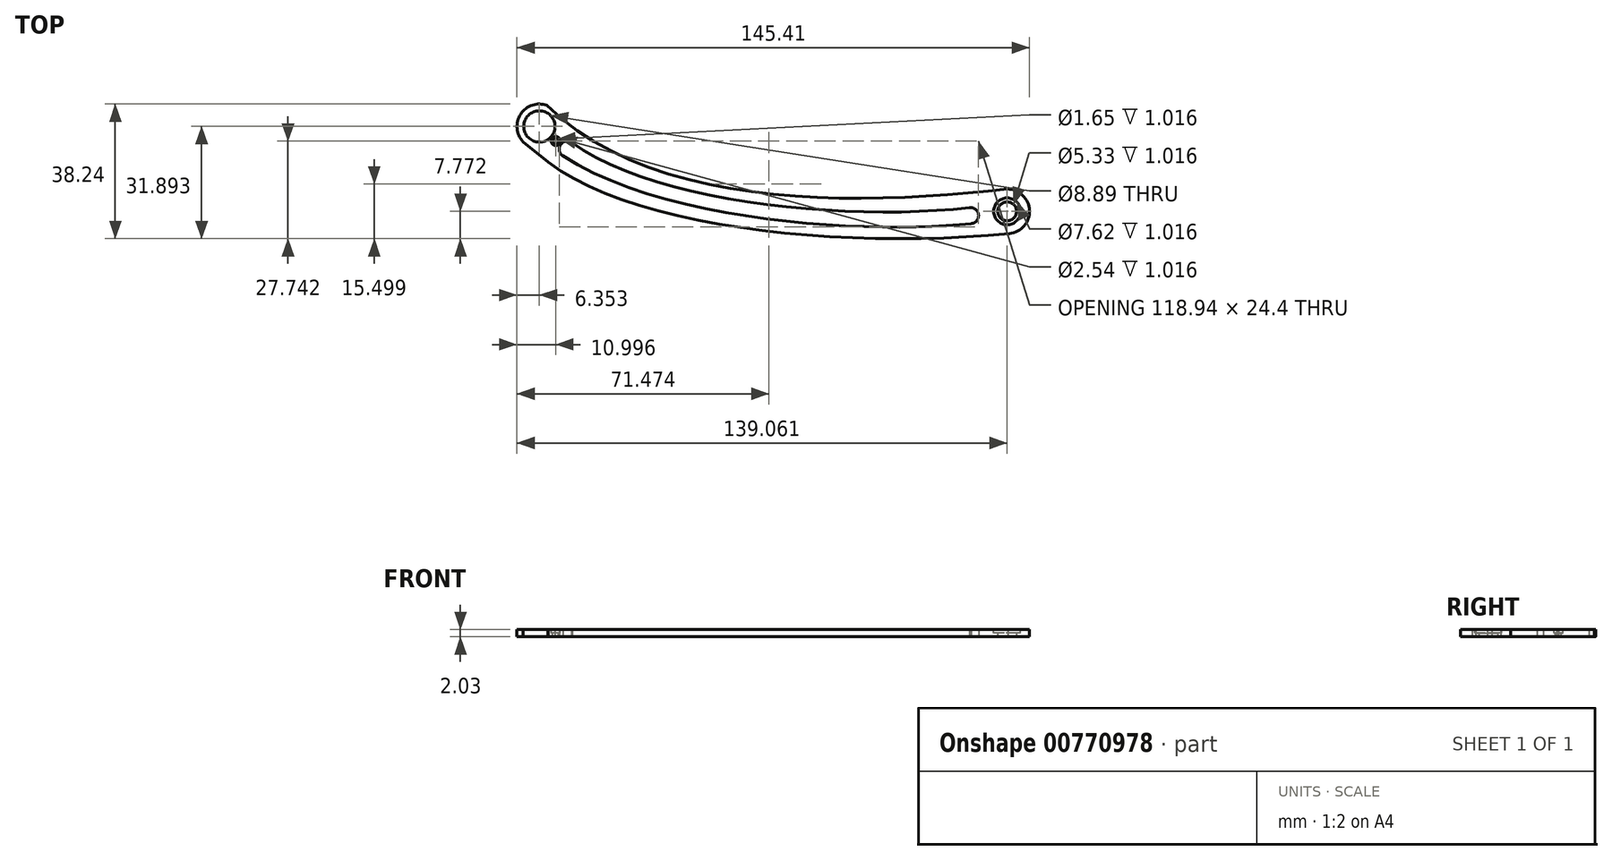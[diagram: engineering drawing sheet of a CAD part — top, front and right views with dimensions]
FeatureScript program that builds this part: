
annotation { "Feature Type Name" : "Feature", "Feature Type Description" : "" }
export const myFeature = defineFeature(function(context is Context, id is Id, definition is map)
    precondition{}
    {
        {
            var Q0;
            Q0=qCreatedBy(makeId("Top.planeOp"),FACE);
            var sketch = newSketch(context, id + "F0", { "sketchPlane" : qUnion([Q0])});
            skArc(sketch, "E0", {"start": v(-15, -65.15) * mm, "mid": v(-9.32, -58.57) * mm, "end": v(-15.52, -52.49) * mm});
            skArc(sketch, "E1", {"start": v(-146.22, -28.74) * mm, "mid": v(-153.68, -31.23) * mm, "end": v(-153, -39.07) * mm});
            skFitSpline(sketch, "E2", {"points": [v(-146.22, -28.74) * mm, v(-15.52, -52.49) * mm], "startDerivative": vector(92.44, -90.26) * mm, "endDerivative": vector(125.95, 14.09) * mm});
            skFitSpline(sketch, "E3", {"points": [v(-150.76, -40.6) * mm, v(-15, -65.15) * mm], "startDerivative": vector(65.25, -67.65) * mm, "endDerivative": vector(148.54, 14.43) * mm});
            skLineSegment(sketch, "E4", {"start": v(-153, -39.07) * mm, "end": v(-145.87, -44.9) * mm});
            skCircle(sketch, "E5", {"center": v(-148.38, -34.72) * mm, "radius": 4.45 * mm});
            skCircle(sketch, "E6", {"center": v(-15.67, -58.84) * mm, "radius": 2.67 * mm});
            skArc(sketch, "E7", {"start": v(-139.03, -39.4) * mm, "mid": v(-139.15, -39.3) * mm, "end": v(-139.27, -39.2) * mm});
            skArc(sketch, "E8", {"start": v(-25.87, -62.31) * mm, "mid": v(-23.78, -59.76) * mm, "end": v(-26.41, -57.78) * mm});
            skFitSpline(sketch, "E9", {"points": [v(-139.27, -39.2) * mm, v(-26.24, -57.75) * mm], "startDerivative": vector(69.49, -51.74) * mm, "endDerivative": vector(101.38, 12.17) * mm});
            skFitSpline(sketch, "E10", {"points": [v(-25.87, -62.31) * mm, v(-141.74, -43.12) * mm], "startDerivative": vector(-72.87, -8.27) * mm, "endDerivative": vector(-94.2, 60.5) * mm});
            skArc(sketch, "E11", {"start": v(-139.27, -39.2) * mm, "mid": v(-142.4, -39.97) * mm, "end": v(-141.74, -43.12) * mm});
            skSolve(sketch);
        }
        {
            var Q0;
            {var subQ10=sQuery(id+"F0.wireOp",EDGE,"E0");Q0=makeQuery(id+"F0.imprint","IMPRINT",FACE,{"disambiguationData":[TD([[makeQuery(id+"F0.imprint","IMPRINT",EDGE,{"derivedFrom":subQ10}),1.0]])]});}
            extrude(context, id + "F1", {"entities" : qUnion([Q0]), "depth" : 2.03 * mm, "offsetDistance" : 25.4 * mm});
        }
        {
            var Q0;
            Q0=makeQuery(id+"F1.opExtrude","CAP_FACE",FACE,{"disambiguationData":[OSD([sQuery(id+"F0.wireOp",EDGE,"E0"),sQuery(id+"F0.wireOp",EDGE,"E1"),sQuery(id+"F0.wireOp",EDGE,"E2"),sQuery(id+"F0.wireOp",EDGE,"E3"),sQuery(id+"F0.wireOp",EDGE,"E4"),sQuery(id+"F0.wireOp",EDGE,"E5"),sQuery(id+"F0.wireOp",EDGE,"E6"),sQuery(id+"F0.wireOp",EDGE,"E7"),sQuery(id+"F0.wireOp",EDGE,"E8"),sQuery(id+"F0.wireOp",EDGE,"E9"),sQuery(id+"F0.wireOp",EDGE,"E10"),sQuery(id+"F0.wireOp",EDGE,"E11")])],"isStart":false});
            var sketch = newSketch(context, id + "F2", { "sketchPlane" : qUnion([Q0])});
            skCircle(sketch, "E12", {"center": v(-15.67, -58.84) * mm, "radius": 3.81 * mm});
            skSolve(sketch);
        }
        {
            var Q0;
            Q0=makeQuery(id+"F2.imprint","IMPRINT",FACE,{"disambiguationData":[TD([[makeQuery(id+"F2.imprint","IMPRINT",EDGE,{"derivedFrom":sQuery(id+"F2.wireOp",EDGE,"E12")}),1.0]])]});
            extrude(context, id + "F3", {"entities" : qUnion([Q0]), "operationType" : NewBodyOperationType.REMOVE, "oppositeDirection" : true, "depth" : 1.02 * mm, "offsetDistance" : 25.4 * mm});
        }
        {
            var Q0;
            Q0=makeQuery(id+"F1.opExtrude","CAP_FACE",FACE,{"disambiguationData":[OSD([sQuery(id+"F0.wireOp",EDGE,"E0"),sQuery(id+"F0.wireOp",EDGE,"E1"),sQuery(id+"F0.wireOp",EDGE,"E2"),sQuery(id+"F0.wireOp",EDGE,"E3"),sQuery(id+"F0.wireOp",EDGE,"E4"),sQuery(id+"F0.wireOp",EDGE,"E5"),sQuery(id+"F0.wireOp",EDGE,"E6"),sQuery(id+"F0.wireOp",EDGE,"E7"),sQuery(id+"F0.wireOp",EDGE,"E8"),sQuery(id+"F0.wireOp",EDGE,"E9"),sQuery(id+"F0.wireOp",EDGE,"E10"),sQuery(id+"F0.wireOp",EDGE,"E11")])],"isStart":false});
            var sketch = newSketch(context, id + "F4", { "sketchPlane" : qUnion([Q0])});
            skCircle(sketch, "E13", {"center": v(-143.73, -38.87) * mm, "radius": 0.83 * mm});
            skSolve(sketch);
        }
        {
            var Q0;
            Q0=makeQuery(id+"F4.imprint","IMPRINT",FACE,{"disambiguationData":[TD([[makeQuery(id+"F4.imprint","IMPRINT",EDGE,{"derivedFrom":sQuery(id+"F4.wireOp",EDGE,"E13")}),1.0]])]});
            extrude(context, id + "F5", {"entities" : qUnion([Q0]), "operationType" : NewBodyOperationType.REMOVE, "oppositeDirection" : true, "depth" : 25.4 * mm, "offsetDistance" : 25.4 * mm});
        }
        {
            var Q0;
            Q0=makeQuery(id+"F1.opExtrude","CAP_FACE",FACE,{"disambiguationData":[OSD([sQuery(id+"F0.wireOp",EDGE,"E0"),sQuery(id+"F0.wireOp",EDGE,"E1"),sQuery(id+"F0.wireOp",EDGE,"E2"),sQuery(id+"F0.wireOp",EDGE,"E3"),sQuery(id+"F0.wireOp",EDGE,"E4"),sQuery(id+"F0.wireOp",EDGE,"E5"),sQuery(id+"F0.wireOp",EDGE,"E6"),sQuery(id+"F0.wireOp",EDGE,"E7"),sQuery(id+"F0.wireOp",EDGE,"E8"),sQuery(id+"F0.wireOp",EDGE,"E9"),sQuery(id+"F0.wireOp",EDGE,"E10"),sQuery(id+"F0.wireOp",EDGE,"E11")])],"isStart":false});
            var sketch = newSketch(context, id + "F6", { "sketchPlane" : qUnion([Q0])});
            skCircle(sketch, "E14", {"center": v(-143.73, -38.87) * mm, "radius": 1.27 * mm});
            skSolve(sketch);
        }
        {
            var Q0;
            Q0=makeQuery(id+"F6.imprint","IMPRINT",FACE,{"disambiguationData":[TD([[makeQuery(id+"F6.imprint","IMPRINT",EDGE,{"derivedFrom":sQuery(id+"F6.wireOp",EDGE,"E14")}),1.0]])]});
            extrude(context, id + "F7", {"entities" : qUnion([Q0]), "operationType" : NewBodyOperationType.REMOVE, "oppositeDirection" : true, "depth" : 1.02 * mm, "offsetDistance" : 25.4 * mm});
        }
    });
